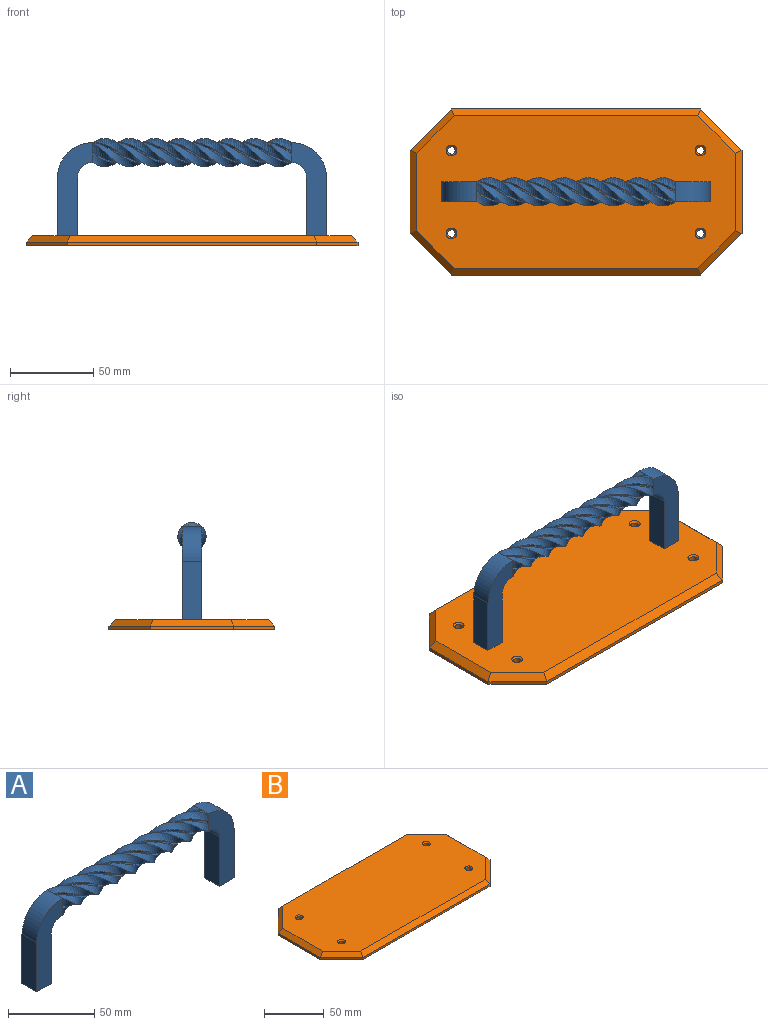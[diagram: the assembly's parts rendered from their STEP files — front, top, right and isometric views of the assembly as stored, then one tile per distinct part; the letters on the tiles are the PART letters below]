
ASSEMBLY  parts=2 mates=1
PART A: 45 faces, bbox 162x20.2x60.3 mm
  f0: bspline ~120x17.3mm, area 666.1mm2, adj f1,f19,f25,f36
  f1: bspline ~120x17.3mm, area 666.1mm2, adj f0,f2,f29,f41
  f2: bspline ~120x12.38mm, area 206mm2, adj f1,f3,f22,f31
  f3: bspline ~120x9.3mm, area 120.1mm2, adj f2,f4,f22,f31
  f4: bspline ~120x12.38mm, area 206mm2, adj f3,f5,f22,f31
  f5: bspline ~120x17.3mm, area 666.1mm2, adj f4,f6,f29,f41
  f6: bspline ~120x17.3mm, area 666.1mm2, adj f5,f7,f27,f38
  f7: bspline ~120x12.38mm, area 206mm2, adj f6,f8,f24,f32
  f8: bspline ~120x9.3mm, area 120.1mm2, adj f7,f9,f24,f32
  f9: bspline ~120x12.11mm, area 206mm2, adj f8,f10,f24,f32
  f10: bspline ~120x17.3mm, area 666.1mm2, adj f9,f11,f27,f38
  f11: bspline ~120x17.3mm, area 666.1mm2, adj f10,f12,f30,f40
  f12: bspline ~120x12.38mm, area 206mm2, adj f11,f13,f21,f35
  f13: bspline ~120x9.3mm, area 120.1mm2, adj f12,f14,f21,f35
  f14: bspline ~120x12.38mm, area 206mm2, adj f13,f15,f21,f35
  f15: bspline ~120x17.3mm, area 666.1mm2, adj f14,f16,f30,f40
  f16: bspline ~120x17.3mm, area 666.1mm2, adj f15,f17,f25,f36
  f17: bspline ~120x12.11mm, area 206mm2, adj f16,f18,f20,f33
  f18: bspline ~120x9.3mm, area 120.1mm2, adj f17,f19,f20,f33
  f19: bspline ~120x12.38mm, area 206mm2, adj f0,f18,f20,f33
  f20: plane 1.65x1.46mm, normal (-1,0,0), area 1.9mm2, adj f17,f18,f19,f25
  f21: plane 1.65x1.46mm, normal (-1,0,0), area 1.9mm2, adj f12,f13,f14,f30
  f22: plane 1.65x1.46mm, normal (-1,0,0), area 1.9mm2, adj f2,f3,f4,f29
  f23: plane 12x12mm, normal (0,0,-1), area 144mm2, adj f25,f26,f27,f28
  f24: plane 1.65x1.46mm, normal (-1,0,0), area 1.9mm2, adj f7,f8,f9,f27
  f25: plane 56x21mm, normal (0,-1,0), area 702.7mm2, adj f0,f16,f20,f23,f26,f28,f29,f30
  f26: plane 35x12mm, normal (1,0,0), area 420mm2, adj f23,f25,f27,f29
  f27: plane 56x21mm, normal (0,1,0), area 702.7mm2, adj f6,f10,f23,f24,f26,f28,f29,f30
  f28: plane 35x12mm, normal (-1,0,0), area 420mm2, adj f23,f25,f27,f30
  f29: cylinder r=21mm len=21mm, axis (0,-1,0), area 395.8mm2, adj f1,f5,f22,f25,f26,f27
  f30: cylinder r=9mm len=12mm, axis (0,-1,0), area 169.6mm2, adj f11,f15,f21,f25,f27,f28
  f31: plane 1.65x1.46mm, normal (1,0,0), area 1.9mm2, adj f2,f3,f4,f41
  f32: plane 1.65x1.46mm, normal (1,0,0), area 1.9mm2, adj f7,f8,f9,f38
  f33: plane 1.65x1.46mm, normal (1,0,0), area 1.9mm2, adj f17,f18,f19,f36
  f34: plane 12x12mm, normal (0,0,-1), area 144mm2, adj f36,f37,f38,f39
  f35: plane 1.65x1.46mm, normal (1,0,0), area 1.9mm2, adj f12,f13,f14,f40
  f36: plane 56x21mm, normal (0,-1,0), area 702.7mm2, adj f0,f16,f33,f34,f37,f39,f40,f41
  f37: plane 35x12mm, normal (1,0,0), area 420mm2, adj f34,f36,f38,f40
  f38: plane 56x21mm, normal (0,1,0), area 702.7mm2, adj f6,f10,f32,f34,f37,f39,f40,f41
  f39: plane 35x12mm, normal (-1,0,0), area 420mm2, adj f34,f36,f38,f41
  f40: cylinder r=9mm len=12mm, axis (0,1,0), area 169.6mm2, adj f11,f15,f35,f36,f37,f38
  f41: cylinder r=21mm len=21mm, axis (0,1,0), area 395.8mm2, adj f1,f5,f31,f36,f38,f39
  f42: plane 9x9mm, normal (1,0,0), area 63.6mm2, adj f44
  f43: plane 9x9mm, normal (-1,0,0), area 63.6mm2, adj f44
  f44: bspline ~120x20.64mm, area 3393.7mm2, adj f42,f43
PART B: 26 faces, bbox 200x100x6 mm
  f0: plane 150x2mm, normal (0,1,0), area 300mm2, adj f5,f7,f9,f13
  f1: plane 50x2mm, normal (-1,0,0), area 100mm2, adj f5,f6,f9,f10
  f2: plane 150x2mm, normal (0,-1,0), area 300mm2, adj f5,f6,f8,f14
  f3: plane 50x2mm, normal (1,0,0), area 100mm2, adj f5,f7,f8,f17
  f4: plane 192x92mm, normal (0,0,1), area 16504.6mm2, adj f10,f11,f12,f13,f14,f15,f16,f17
  f5: plane 200x100mm, normal (0,0,-1), area 18686.4mm2, adj f0,f1,f2,f3,f6,f7,f8,f9
  f6: plane 25x25mm, normal (-0.71,-0.71,0), area 70.7mm2, adj f1,f2,f5,f12
  f7: plane 25x25mm, normal (0.71,0.71,0), area 70.7mm2, adj f0,f3,f5,f15
  f8: plane 25x25mm, normal (0.71,-0.71,0), area 70.7mm2, adj f2,f3,f5,f16
  f9: plane 25x25mm, normal (-0.71,0.71,0), area 70.7mm2, adj f0,f1,f5,f11
  f10: plane 50x4mm, normal (-0.71,0,0.71), area 273.5mm2, adj f1,f4,f11,f12
  f11: plane 26.66x26.66mm, normal (-0.5,0.5,0.71), area 190.6mm2, adj f4,f9,f10,f13
  f12: plane 26.66x26.66mm, normal (-0.5,-0.5,0.71), area 190.6mm2, adj f4,f6,f10,f14
  f13: plane 150x4mm, normal (0,0.71,0.71), area 839.2mm2, adj f0,f4,f11,f15
  f14: plane 150x4mm, normal (0,-0.71,0.71), area 839.2mm2, adj f2,f4,f12,f16
  f15: plane 26.66x26.66mm, normal (0.5,0.5,0.71), area 190.6mm2, adj f4,f7,f13,f17
  f16: plane 26.66x26.66mm, normal (0.5,-0.5,0.71), area 190.6mm2, adj f4,f8,f14,f17
  f17: plane 50x4mm, normal (0.71,0,0.71), area 273.5mm2, adj f3,f4,f15,f16
  f18: cylinder r=2.25mm len=5mm, axis (0,0,1), area 70.7mm2, adj f5,f25
  f19: cylinder r=2.25mm len=5mm, axis (0,0,1), area 70.7mm2, adj f5,f22
  f20: cylinder r=2.25mm len=5mm, axis (0,0,1), area 70.7mm2, adj f5,f23
  f21: cylinder r=2.25mm len=5mm, axis (0,0,1), area 70.7mm2, adj f5,f24
  f22: cone r=2.25mm half-angle=45deg, axis (0,0,1), area 24.4mm2, adj f4,f19
  f23: cone r=2.25mm half-angle=45deg, axis (0,0,1), area 24.4mm2, adj f4,f20
  f24: cone r=2.25mm half-angle=45deg, axis (0,0,1), area 24.4mm2, adj f4,f21
  f25: cone r=2.25mm half-angle=45deg, axis (0,0,1), area 24.4mm2, adj f4,f18
PLACE A t=(15.95,25.26,35.07)mm
PLACE B t=(15.95,25.26,38.56)mm
MATE fastened B.f4 <-> A.f34  axis (0,0,1) through (15.95,25.26,44.56)mm
